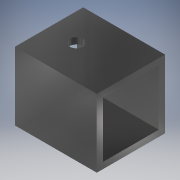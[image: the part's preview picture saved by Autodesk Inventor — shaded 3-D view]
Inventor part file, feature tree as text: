
AUTODESK INVENTOR PART (.ipt)
format: ipt  version: 2018 (Build 220112000, 112)  size: 111,616 bytes
history: native  units: mm
features: extrude x2, sketch x2, other x1
ambient origin geometry x8: Origin, YZ Plane, XZ Plane, XY Plane, X Axis, Y Axis, Z Axis, Center Point
bodies: Body1 (feature_tree)
feature tree (5):
  other  "ソリッド1"
  extrude  "押し出し1"  Depth=25.0mm
  extrude  "押し出し2"  Depth=25.0mm
  sketch  "スケッチ1"
  sketch  "スケッチ2"
